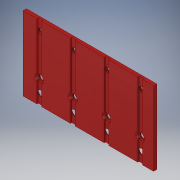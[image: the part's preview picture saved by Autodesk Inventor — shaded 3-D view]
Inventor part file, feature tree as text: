
AUTODESK INVENTOR PART (.ipt)
format: ipt  version: 2019 (Build 230136000, 136)  size: 209,920 bytes
history: native  units: in
note: dims shown in document units (in); Inventor stores cm internally (conversion verified against a paired STEP export)
features: sketch x5, hole x3, projected_geometry x3, extrude x2, pattern_linear x1
ambient origin geometry x8: Origin, YZ Plane, XZ Plane, XY Plane, X Axis, Y Axis, Z Axis, Center Point
bodies: Solid1 (feature_tree)
feature tree (14):
  extrude  "Extrusion1"  Depth=4.85in
  hole  "Hole1"  [1 undecoded]
  hole  "Hole2"  [1 undecoded]
  hole  "Hole3"  [1 undecoded]
  extrude  "Extrusion2"  Depth=0.177in
  pattern_linear  "Rectangular Pattern1"  Spacing1=0.05in  [1 undecoded]
  sketch  "Sketch1"  dims[d0=2.75in d1=4.85in]
  sketch  "Sketch2"  dims[d2=0.125in d3=0.0in d5=0.385in]
  sketch  "Sketch3"  dims[d6=0.6in d7=1.25in]
  projected_geometry  "Projected Loop1"
  sketch  "Sketch4"  dims[d8=1.25in d9=1.25in]
  projected_geometry  "Projected Loop2"
  sketch  "Sketch5"  dims[d10=0.177in d11=0.75in d12=0.385in d13=0.25in d14=0.5635in d15=1.0in d16=0.8108in d19=0.177in d20=1.717in d21=0.332in d22=0.25in d23=0.5635in d24=1.0in d25=0.8108in d26=2.0in d27=0.177in d28=1.717in d29=0.332in d30=0.25in d31=0.5635in d32=1.0in d33=0.8108in d34=0.05in d35=0.0in d36=1.5748in d38=1.25in]
  projected_geometry  "Projected Loop3"
note: 4 required parameter values undecoded (feature->parameter linkage not recoverable at this tier; creation-order binding heuristic only, values carry confidence <= 0.55)
